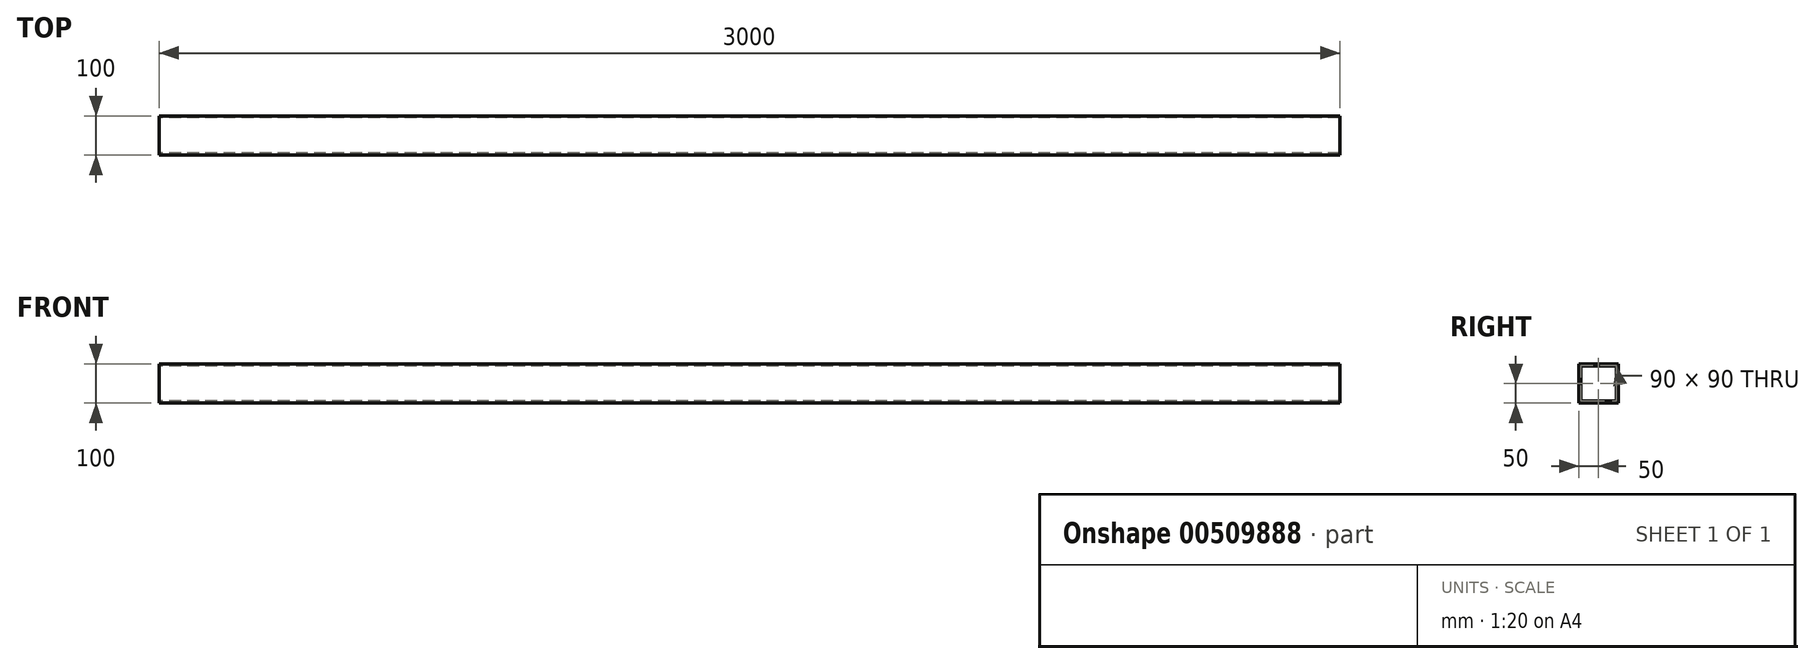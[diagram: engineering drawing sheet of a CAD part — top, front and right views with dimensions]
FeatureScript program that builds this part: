
annotation { "Feature Type Name" : "Feature", "Feature Type Description" : "" }
export const myFeature = defineFeature(function(context is Context, id is Id, definition is map)
    precondition{}
    {
        {
            var Q0;
            Q0=qCreatedBy(makeId("Right.planeOp"),FACE);
            var sketch = newSketch(context, id + "F0", { "sketchPlane" : qUnion([Q0])});
            skLineSegment(sketch, "E0.bottom", {"start": v(50, -50) * mm, "end": v(-50, -50) * mm});
            skLineSegment(sketch, "E0.top", {"start": v(50, 50) * mm, "end": v(-50, 50) * mm});
            skLineSegment(sketch, "E0.left", {"start": v(50, -50) * mm, "end": v(50, 50) * mm});
            skLineSegment(sketch, "E0.right", {"start": v(-50, -50) * mm, "end": v(-50, 50) * mm});
            skPoint(sketch, "E0.middle", {"position": v(0, 0) * mm});
            skLineSegment(sketch, "E1.bottom", {"start": v(45, -45) * mm, "end": v(-45, -45) * mm});
            skLineSegment(sketch, "E1.top", {"start": v(45, 45) * mm, "end": v(-45, 45) * mm});
            skLineSegment(sketch, "E1.left", {"start": v(45, -45) * mm, "end": v(45, 45) * mm});
            skLineSegment(sketch, "E1.right", {"start": v(-45, -45) * mm, "end": v(-45, 45) * mm});
            skSolve(sketch);
        }
        {
            var Q0;
            Q0=makeQuery(id+"F0.imprint","IMPRINT",FACE,{"disambiguationData":[TD([[makeQuery(id+"F0.imprint","IMPRINT",EDGE,{"derivedFrom":sQuery(id+"F0.wireOp",EDGE,"E0.bottom")}),-1.0]])]});
            extrude(context, id + "F1", {"entities" : qUnion([Q0]), "depth" : 3000 * mm, "offsetDistance" : 25 * mm});
        }
    });
